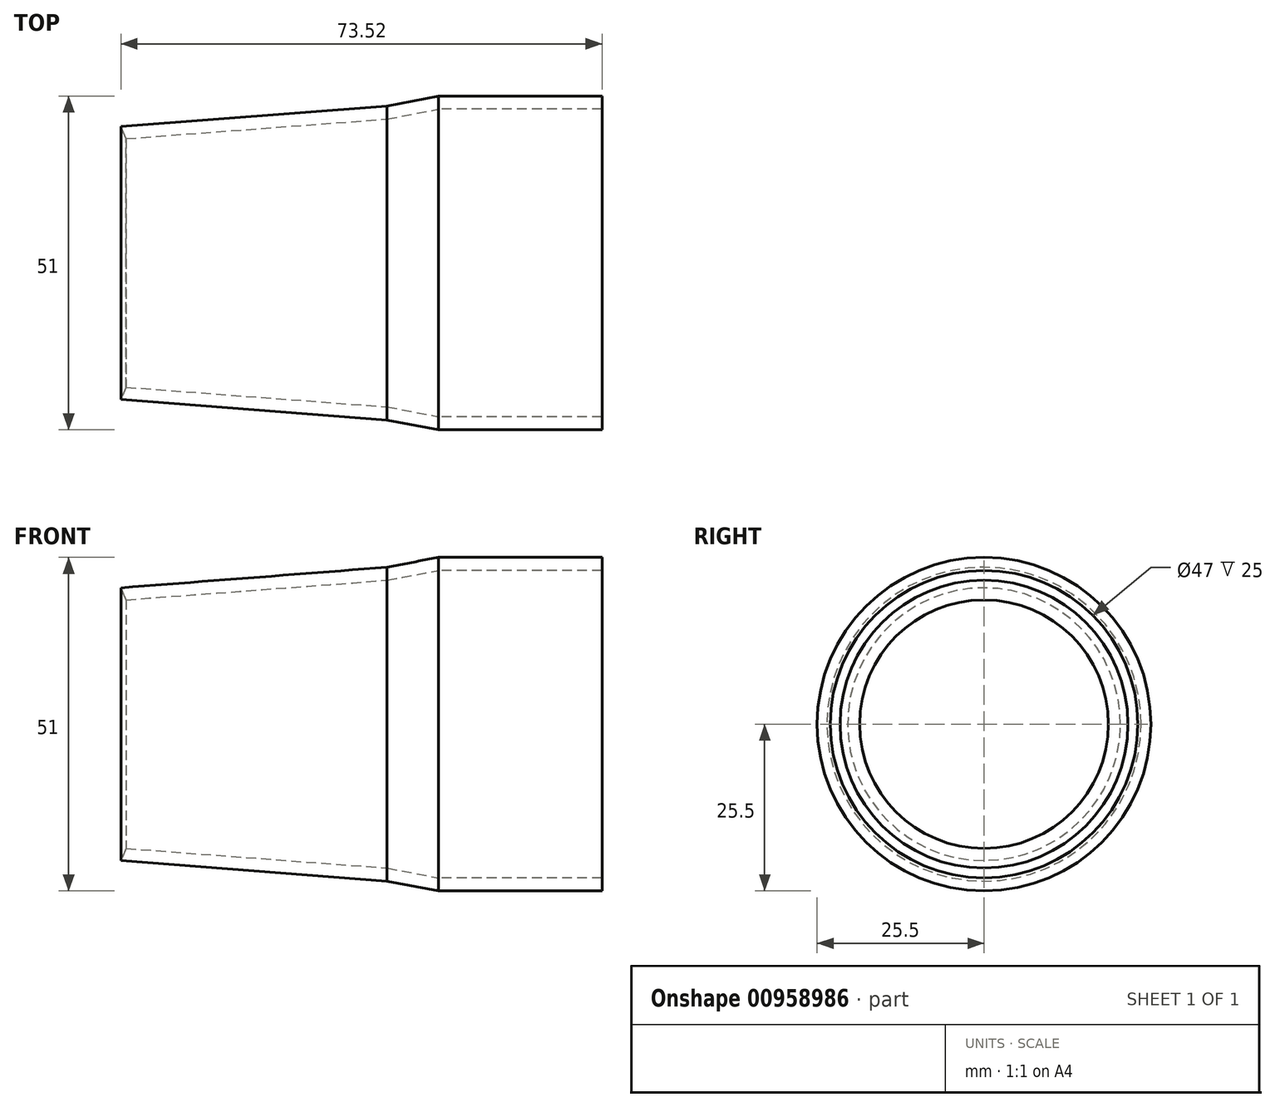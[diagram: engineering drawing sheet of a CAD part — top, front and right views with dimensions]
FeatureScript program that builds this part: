
annotation { "Feature Type Name" : "Feature", "Feature Type Description" : "" }
export const myFeature = defineFeature(function(context is Context, id is Id, definition is map)
    precondition{}
    {
        {
            var Q0;
            Q0=qCreatedBy(makeId("Top.planeOp"),FACE);
            var sketch = newSketch(context, id + "F0", { "sketchPlane" : qUnion([Q0])});
            skLineSegment(sketch, "E0", {"start": v(24.13, 23.5) * mm, "end": v(16.28, 22) * mm});
            skLineSegment(sketch, "E1", {"start": v(-43.34, 0) * mm, "end": v(39.1, 0) * mm, "construction": true});
            skLineSegment(sketch, "E2", {"start": v(24.13, 25.5) * mm, "end": v(49.13, 25.5) * mm});
            skLineSegment(sketch, "E3", {"start": v(49.13, 25.5) * mm, "end": v(49.13, 23.5) * mm});
            skLineSegment(sketch, "E4", {"start": v(49.13, 23.5) * mm, "end": v(24.13, 23.5) * mm});
            skPoint(sketch, "E5", {"position": v(49.13, 23.5) * mm});
            skPoint(sketch, "E6", {"position": v(36.63, 23.5) * mm});
            skPoint(sketch, "E7", {"position": v(24.13, 23.5) * mm});
            skLineSegment(sketch, "E8", {"start": v(49.13, 23.5) * mm, "end": v(49.13, 0) * mm, "construction": true});
            skLineSegment(sketch, "E9", {"start": v(24.13, 25.5) * mm, "end": v(24.13, 23.5) * mm, "construction": true});
            skLineSegment(sketch, "E10", {"start": v(24.13, 23.5) * mm, "end": v(24.13, 0) * mm, "construction": true});
            skPoint(sketch, "E11.endSnap0", {"position": v(-2.12, 0) * mm});
            skLineSegment(sketch, "E12", {"start": v(16.28, 22) * mm, "end": v(16.28, 0) * mm, "construction": true});
            skLineSegment(sketch, "E13", {"start": v(16.28, 22) * mm, "end": v(16.27, 24) * mm, "construction": true});
            skLineSegment(sketch, "E14", {"start": v(16.27, 24) * mm, "end": v(24.13, 25.5) * mm});
            skLineSegment(sketch, "E15", {"start": v(16.28, 22) * mm, "end": v(-23.6, 19) * mm});
            skLineSegment(sketch, "E16", {"start": v(-23.6, 19) * mm, "end": v(-23.6, 0) * mm, "construction": true});
            skLineSegment(sketch, "E17", {"start": v(-23.6, 19) * mm, "end": v(-24.39, 20.84) * mm});
            skLineSegment(sketch, "E18", {"start": v(-24.39, 20.84) * mm, "end": v(16.27, 24) * mm});
            skSolve(sketch);
        }
        {
            var Q0;
            Q0=makeQuery(id+"F0.imprint","IMPRINT",FACE,{"disambiguationData":[TD([[makeQuery(id+"F0.imprint","IMPRINT",EDGE,{"derivedFrom":sQuery(id+"F0.wireOp",EDGE,"E0")}),-1.0]])]});
            var Q1;
            Q1=sQuery(id+"F0.wireOp",EDGE,"E1");
            revolve(context, id + "F1", {"surfaceOperationType" : NewSurfaceOperationType.NEW, "entities" : qUnion([Q0]), "axis" : qUnion([Q1]), "revolveType" : RevolveType.FULL});
        }
    });
